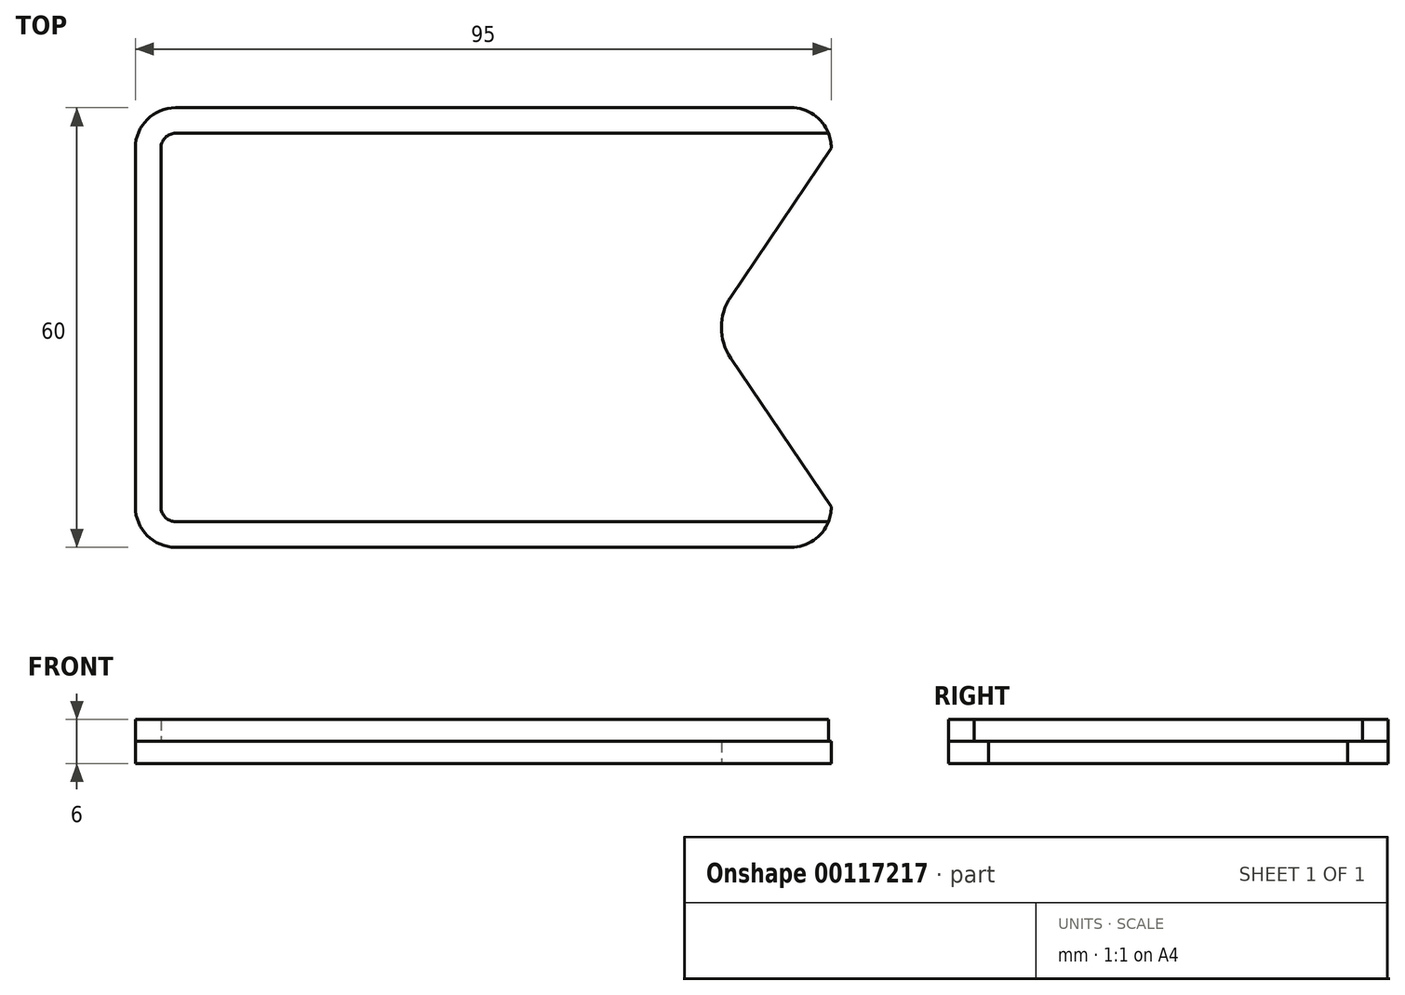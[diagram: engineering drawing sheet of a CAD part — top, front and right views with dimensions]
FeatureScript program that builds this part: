
annotation { "Feature Type Name" : "Feature", "Feature Type Description" : "" }
export const myFeature = defineFeature(function(context is Context, id is Id, definition is map)
    precondition{}
    {
        {
            var Q0;
            Q0=qCreatedBy(makeId("Top.planeOp"),FACE);
            var sketch = newSketch(context, id + "F0", { "sketchPlane" : qUnion([Q0])});
            skLineSegment(sketch, "E0.bottom", {"start": v(42, -30) * mm, "end": v(-42, -30) * mm});
            skLineSegment(sketch, "E0.top", {"start": v(42, 30) * mm, "end": v(-42, 30) * mm});
            skLineSegment(sketch, "E0.left", {"start": v(47.5, -24.5) * mm, "end": v(47.5, 24.5) * mm});
            skLineSegment(sketch, "E0.right", {"start": v(-47.5, -24.5) * mm, "end": v(-47.5, 24.5) * mm});
            skPoint(sketch, "E0.middle", {"position": v(0, 0) * mm});
            skPoint(sketch, "E1.visualSharp", {"position": v(-47.5, 30) * mm});
            skArc(sketch, "E1.filletArc", {"start": v(-42, 30) * mm, "mid": v(-45.89, 28.39) * mm, "end": v(-47.5, 24.5) * mm});
            skPoint(sketch, "E2.visualSharp", {"position": v(-47.5, -30) * mm});
            skArc(sketch, "E2.filletArc", {"start": v(-47.5, -24.5) * mm, "mid": v(-45.89, -28.39) * mm, "end": v(-42, -30) * mm});
            skPoint(sketch, "E3.visualSharp", {"position": v(47.5, -30) * mm});
            skArc(sketch, "E3.filletArc", {"start": v(42, -30) * mm, "mid": v(45.89, -28.39) * mm, "end": v(47.5, -24.5) * mm});
            skPoint(sketch, "E4.visualSharp", {"position": v(47.5, 30) * mm});
            skArc(sketch, "E4.filletArc", {"start": v(47.5, 24.5) * mm, "mid": v(45.89, 28.39) * mm, "end": v(42, 30) * mm});
            skArc(sketch, "E5.0", {"start": v(-44, -24.5) * mm, "mid": v(-43.41, -25.91) * mm, "end": v(-42, -26.5) * mm});
            skLineSegment(sketch, "E5.1", {"start": v(47.5, -26.5) * mm, "end": v(-42, -26.5) * mm});
            skLineSegment(sketch, "E5.2", {"start": v(-44, -24.5) * mm, "end": v(-44, 24.5) * mm});
            skArc(sketch, "E5.4", {"start": v(-42, 26.5) * mm, "mid": v(-43.41, 25.91) * mm, "end": v(-44, 24.5) * mm});
            skLineSegment(sketch, "E5.5", {"start": v(47.5, 26.5) * mm, "end": v(-42, 26.5) * mm});
            skSolve(sketch);
        }
        {
            var Q0;
            {var subQ8=sQuery(id+"F0.wireOp",EDGE,"E0.bottom");Q0=makeQuery(id+"F0.imprint","IMPRINT",FACE,{"disambiguationData":[TD([[makeQuery(id+"F0.imprint","IMPRINT",EDGE,{"derivedFrom":subQ8}),-1.0]])]});}
            var Q1;
            {var subQ2=sQuery(id+"F0.wireOp",EDGE,"E0.left");Q1=makeQuery(id+"F0.imprint","IMPRINT",FACE,{"disambiguationData":[TD([[makeQuery(id+"F0.imprint","IMPRINT",EDGE,{"derivedFrom":subQ2}),1.0]])]});}
            extrude(context, id + "F1", {"entities" : qUnion([Q0, Q1]), "oppositeDirection" : true, "depth" : 3 * mm});
        }
        {
            var Q0;
            {var subQ8=sQuery(id+"F0.wireOp",EDGE,"E0.bottom");Q0=makeQuery(id+"F0.imprint","IMPRINT",FACE,{"disambiguationData":[TD([[makeQuery(id+"F0.imprint","IMPRINT",EDGE,{"derivedFrom":subQ8}),-1.0]])]});}
            extrude(context, id + "F2", {"entities" : qUnion([Q0]), "depth" : 3 * mm});
        }
        {
            var Q0;
            Q0=makeQuery(id+"F1.opExtrude","CAP_FACE",FACE,{"disambiguationData":[OSD([sQuery(id+"F0.wireOp",EDGE,"E0.bottom"),sQuery(id+"F0.wireOp",EDGE,"E0.top"),sQuery(id+"F0.wireOp",EDGE,"E0.left"),sQuery(id+"F0.wireOp",EDGE,"E0.right"),sQuery(id+"F0.wireOp",EDGE,"E1.filletArc"),sQuery(id+"F0.wireOp",EDGE,"E2.filletArc"),sQuery(id+"F0.wireOp",EDGE,"E3.filletArc"),sQuery(id+"F0.wireOp",EDGE,"E4.filletArc")])],"isStart":false});
            var sketch = newSketch(context, id + "F3", { "sketchPlane" : qUnion([Q0])});
            skLineSegment(sketch, "E6", {"start": v(47.5, 0) * mm, "end": v(2.32, 0) * mm, "construction": true});
            skPoint(sketch, "E6.endSnap0", {"position": v(47.5, 0) * mm});
            skArc(sketch, "E7", {"start": v(33.79, 4.2) * mm, "mid": v(32.5, 0) * mm, "end": v(33.79, -4.2) * mm});
            skLineSegment(sketch, "E8", {"start": v(47.5, 24.5) * mm, "end": v(33.79, 4.2) * mm});
            skLineSegment(sketch, "E9", {"start": v(47.5, -24.5) * mm, "end": v(33.79, -4.2) * mm});
            skSolve(sketch);
        }
        {
            var Q0;
            Q0 = qSketchRegion(id + "F3", true);
            var Q1;
            Q1=makeQuery(id+"F3.imprint","IMPRINT",FACE,{"disambiguationData":[TD([[makeQuery(id+"F3.imprint","IMPRINT",EDGE,{"derivedFrom":sQuery(id+"F3.wireOp",EDGE,"E7")}),1.0]])]});
            extrude(context, id + "F4", {"entities" : qUnion([Q0, Q1]), "operationType" : NewBodyOperationType.REMOVE, "oppositeDirection" : true, "depth" : 25 * mm});
        }
    });
